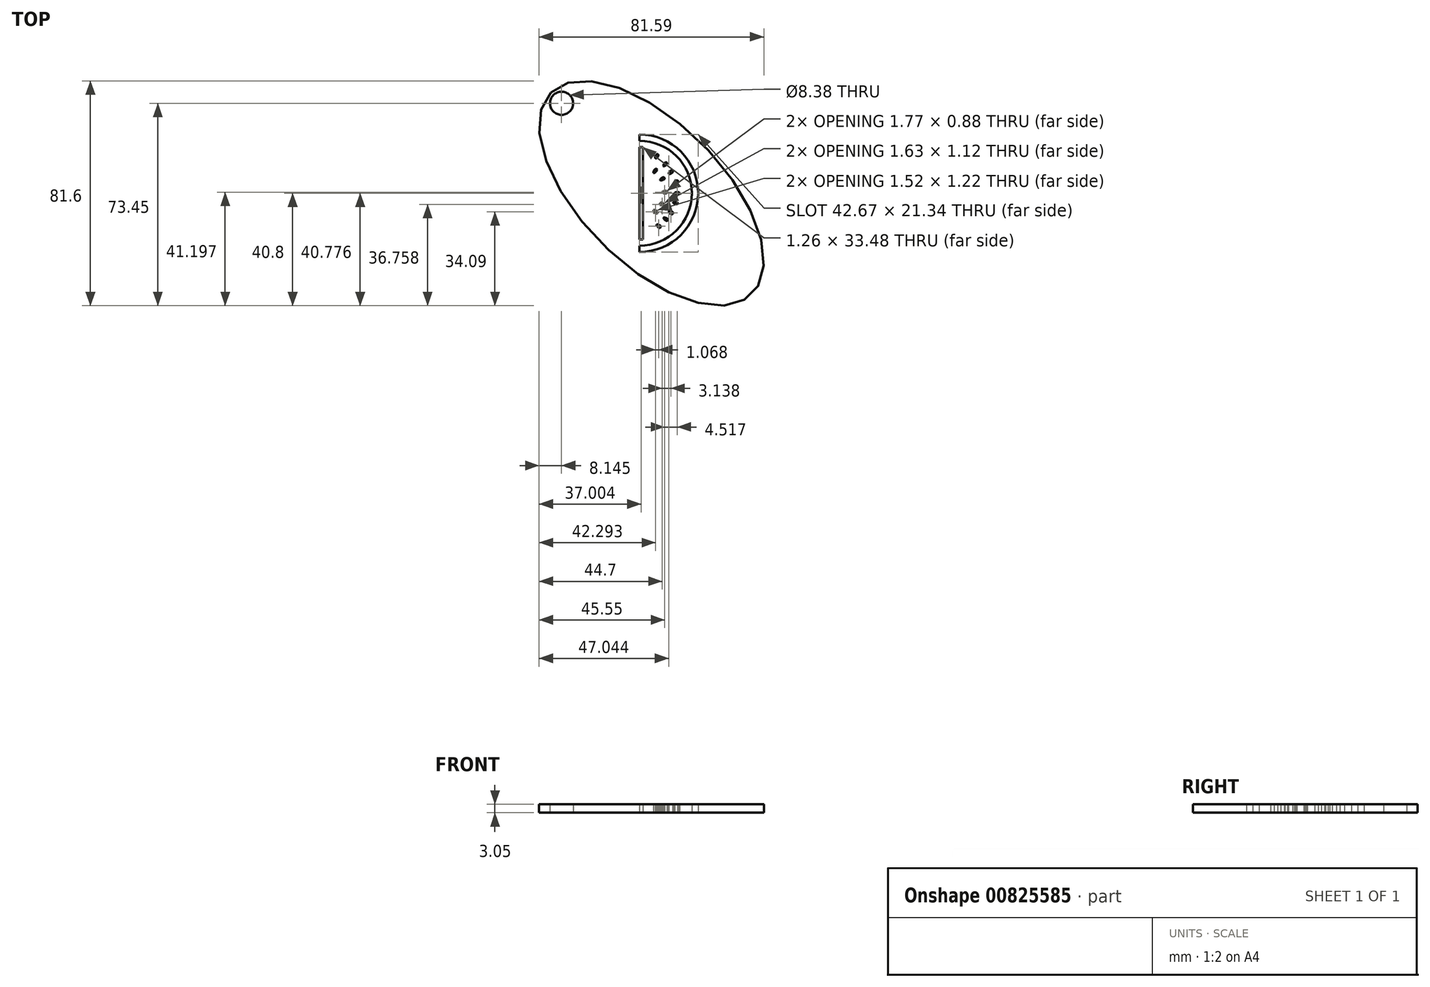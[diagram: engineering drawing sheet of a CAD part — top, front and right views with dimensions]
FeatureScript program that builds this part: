
annotation { "Feature Type Name" : "Feature", "Feature Type Description" : "" }
export const myFeature = defineFeature(function(context is Context, id is Id, definition is map)
    precondition{}
    {
        {
            var Q0;
            Q0=qCreatedBy(makeId("Top.planeOp"),FACE);
            var sketch = newSketch(context, id + "F0", { "sketchPlane" : qUnion([Q0])});
            skCircle(sketch, "E0", {"center": v(0, 0) * mm, "radius": 35.56 * mm});
            skCircle(sketch, "E1", {"center": v(0, 0) * mm, "radius": 31.75 * mm});
            skCircle(sketch, "E2", {"center": v(0, 0) * mm, "radius": 27.94 * mm, "construction": true});
            skLineSegment(sketch, "E3", {"start": v(-35.56, 0) * mm, "end": v(-31.75, 0) * mm, "construction": true});
            skLineSegment(sketch, "E4", {"start": v(-31.75, 0) * mm, "end": v(-27.94, 0) * mm, "construction": true});
            skLineSegment(sketch, "E5", {"start": v(0, 0) * mm, "end": v(0, 27.94) * mm});
            skLineSegment(sketch, "E6", {"start": v(0, -35.56) * mm, "end": v(0, -31.75) * mm});
            skLineSegment(sketch, "E7", {"start": v(0, -31.75) * mm, "end": v(0, -27.94) * mm});
            skLineSegment(sketch, "E8", {"start": v(0, -27.94) * mm, "end": v(0, 0) * mm});
            skLineSegment(sketch, "E9", {"start": v(0, 35.56) * mm, "end": v(0, 31.75) * mm});
            skLineSegment(sketch, "E10", {"start": v(0, 31.75) * mm, "end": v(0, 27.94) * mm});
            skLineSegment(sketch, "E11.bottom", {"start": v(0, 27.94) * mm, "end": v(0, 27.94) * mm});
            skLineSegment(sketch, "E11.top", {"start": v(0, -27.94) * mm, "end": v(0, -27.94) * mm});
            skLineSegment(sketch, "E11.left", {"start": v(0, 27.94) * mm, "end": v(0, -27.94) * mm});
            skLineSegment(sketch, "E11.right", {"start": v(0, 27.94) * mm, "end": v(0, -27.94) * mm});
            skLineSegment(sketch, "E12", {"start": v(0, 0) * mm, "end": v(17.78, 0) * mm, "construction": true});
            skLineSegment(sketch, "E13", {"start": v(17.78, 0) * mm, "end": v(35.56, 0) * mm, "construction": true});
            skLineSegment(sketch, "E14", {"start": v(0, 35.56) * mm, "end": v(-35.56, 0) * mm, "construction": true});
            skLineSegment(sketch, "E15", {"start": v(-35.56, 0) * mm, "end": v(0, -35.56) * mm, "construction": true});
            skLineSegment(sketch, "E16", {"start": v(7.36, -42.92) * mm, "end": v(50.29, 0) * mm, "construction": true});
            skLineSegment(sketch, "E17", {"start": v(7.36, 42.92) * mm, "end": v(50.29, 0) * mm, "construction": true});
            skLineSegment(sketch, "E18", {"start": v(0, -35.56) * mm, "end": v(7.36, -42.92) * mm, "construction": true});
            skLineSegment(sketch, "E19", {"start": v(0, 35.56) * mm, "end": v(7.36, 42.92) * mm, "construction": true});
            skLineSegment(sketch, "E20", {"start": v(7.36, -42.92) * mm, "end": v(7.36, 42.92) * mm, "construction": true});
            skPoint(sketch, "E21", {"position": v(7.36, 0) * mm});
            skLineSegment(sketch, "E22", {"start": v(7.36, 0) * mm, "end": v(37.6, 30.24) * mm, "construction": true});
            skLineSegment(sketch, "E23", {"start": v(7.36, 0) * mm, "end": v(-22.87, -30.24) * mm, "construction": true});
            skLineSegment(sketch, "E24", {"start": v(7.36, 0) * mm, "end": v(68.27, -60.9) * mm, "construction": true});
            skLineSegment(sketch, "E25.bottom", {"start": v(0, -27.94) * mm, "end": v(2.1, -27.94) * mm});
            skLineSegment(sketch, "E25.top", {"start": v(0, 27.86) * mm, "end": v(2.1, 27.86) * mm});
            skLineSegment(sketch, "E25.left", {"start": v(0, -27.94) * mm, "end": v(0, 27.86) * mm});
            skLineSegment(sketch, "E25.right", {"start": v(2.1, -27.94) * mm, "end": v(2.1, 27.86) * mm});
            skPoint(sketch, "E26", {"position": v(-22.87, -30.24) * mm});
            skPoint(sketch, "E27", {"position": v(37.6, 30.24) * mm});
            skPoint(sketch, "E28", {"position": v(-53.54, 60.9) * mm});
            skPoint(sketch, "E29", {"position": v(68.27, -60.9) * mm});
            skEllipse(sketch, "E30", {"center": v(7.36, 0) * mm, "majorRadius": 86.13 * mm, "minorRadius": 42.76 * mm, "majorAxis": v(-0.7, 0.7)});
            skFitSpline(sketch, "E31", {"points": [v(10.37, -18.9) * mm, v(11.47, -20.6) * mm, v(12.55, -20.89) * mm, v(12.77, -19.78) * mm, v(10.37, -18.9) * mm]});
            skFitSpline(sketch, "E32", {"points": [v(17.74, -11.01) * mm, v(19.11, -12.49) * mm, v(20.23, -12.58) * mm, v(20.26, -11.46) * mm, v(17.74, -11.01) * mm]});
            skFitSpline(sketch, "E33", {"points": [v(14.63, -14.82) * mm, v(15.87, -16.4) * mm, v(16.98, -16.6) * mm, v(17.1, -15.49) * mm, v(14.63, -14.82) * mm]});
            skFitSpline(sketch, "E34", {"points": [v(20.26, -5.4) * mm, v(21.92, -6.53) * mm, v(23.03, -6.38) * mm, v(22.8, -5.28) * mm, v(20.26, -5.4) * mm]});
            skFitSpline(sketch, "E35", {"points": [v(21.34, 0) * mm, v(23.21, -0.75) * mm, v(24.26, -0.37) * mm, v(23.81, 0.66) * mm, v(21.34, 0) * mm]});
            skFitSpline(sketch, "E36", {"points": [v(20.86, 5.99) * mm, v(22.85, 6.27) * mm, v(23.57, 7.13) * mm, v(22.66, 7.8) * mm, v(20.86, 5.99) * mm]});
            skFitSpline(sketch, "E37", {"points": [v(8.6, -10.17) * mm, v(9.69, -11.86) * mm, v(10.77, -12.15) * mm, v(11, -11.05) * mm, v(8.6, -10.17) * mm]});
            skFitSpline(sketch, "E38", {"points": [v(12.51, -5.96) * mm, v(13.88, -7.43) * mm, v(15, -7.53) * mm, v(15.03, -6.4) * mm, v(12.51, -5.96) * mm]});
            skFitSpline(sketch, "E39", {"points": [v(13.82, 0.66) * mm, v(15.68, -0.1) * mm, v(16.74, 0.29) * mm, v(16.28, 1.32) * mm, v(13.82, 0.66) * mm]});
            skFitSpline(sketch, "E40", {"points": [v(12.55, 8) * mm, v(14.56, 8.19) * mm, v(15.32, 9.01) * mm, v(14.44, 9.72) * mm, v(12.55, 8) * mm]});
            skFitSpline(sketch, "E41", {"points": [v(17.78, 11.72) * mm, v(19.7, 12.35) * mm, v(20.25, 13.32) * mm, v(19.25, 13.81) * mm, v(17.78, 11.72) * mm]});
            skFitSpline(sketch, "E42", {"points": [v(14.6, 16.37) * mm, v(16.38, 17.31) * mm, v(16.76, 18.37) * mm, v(15.68, 18.68) * mm, v(14.6, 16.37) * mm]});
            skFitSpline(sketch, "E43", {"points": [v(8.6, 12.31) * mm, v(10.33, 13.32) * mm, v(10.68, 14.4) * mm, v(9.59, 14.66) * mm, v(8.6, 12.31) * mm]});
            skFitSpline(sketch, "E44", {"points": [v(9.69, 21.06) * mm, v(11.27, 22.3) * mm, v(11.47, 23.4) * mm, v(10.35, 23.52) * mm, v(9.69, 21.06) * mm]});
            skLineSegment(sketch, "E45", {"start": v(-53.54, 60.9) * mm, "end": v(-52, 59.36) * mm});
            skLineSegment(sketch, "E46", {"start": v(-53.54, 60.9) * mm, "end": v(7.36, 0) * mm, "construction": true});
            skCircle(sketch, "E47", {"center": v(-47.05, 54.42) * mm, "radius": 6.99 * mm});
            skSolve(sketch);
        }
        {
            var Q0;
            Q0=makeQuery(id+"F0.imprint","IMPRINT",FACE,{"disambiguationData":[TD([[makeQuery(id+"F0.imprint","IMPRINT",EDGE,{"derivedFrom":sQuery(id+"F0.wireOp",EDGE,"E30")}),1.0]])]});
            var Q1;
            {var subQ0=sQuery(id+"F0.wireOp",EDGE,"E6");Q1=makeQuery(id+"F0.imprint","IMPRINT",FACE,{"disambiguationData":[TD([[makeQuery(id+"F0.imprint","IMPRINT",EDGE,{"derivedFrom":subQ0}),1.0]])]});}
            var Q2;
            {var subQ0=sQuery(id+"F0.wireOp",EDGE,"E7");Q2=makeQuery(id+"F0.imprint","IMPRINT",FACE,{"disambiguationData":[TD([[makeQuery(id+"F0.imprint","IMPRINT",EDGE,{"derivedFrom":subQ0}),1.0]])]});}
            var Q3;
            {var subQ1=sQuery(id+"F0.wireOp",EDGE,"E7");Q3=makeQuery(id+"F0.imprint","IMPRINT",FACE,{"disambiguationData":[TD([[makeQuery(id+"F0.imprint","IMPRINT",EDGE,{"derivedFrom":subQ1}),-1.0]])]});}
            extrude(context, id + "F1", {"entities" : qUnion([Q0, Q1, Q2, Q3]), "depth" : 5.08 * mm, "offsetDistance" : 25.4 * mm});
        }
        {
            var Q0;
            Q0=makeQuery(id+"F1.opExtrude","SWEPT_BODY",BODY,{"disambiguationData":[OSD([sQuery(id+"F0.wireOp",EDGE,"E0"),sQuery(id+"F0.wireOp",EDGE,"E1"),sQuery(id+"F0.wireOp",EDGE,"E6"),sQuery(id+"F0.wireOp",EDGE,"E9"),sQuery(id+"F0.wireOp",EDGE,"E25.bottom"),sQuery(id+"F0.wireOp",EDGE,"E25.top"),sQuery(id+"F0.wireOp",EDGE,"E25.left"),sQuery(id+"F0.wireOp",EDGE,"E25.right"),sQuery(id+"F0.wireOp",EDGE,"E30"),sQuery(id+"F0.wireOp",EDGE,"E31"),sQuery(id+"F0.wireOp",EDGE,"E32"),sQuery(id+"F0.wireOp",EDGE,"E33"),sQuery(id+"F0.wireOp",EDGE,"E34"),sQuery(id+"F0.wireOp",EDGE,"E35"),sQuery(id+"F0.wireOp",EDGE,"E36"),sQuery(id+"F0.wireOp",EDGE,"E37"),sQuery(id+"F0.wireOp",EDGE,"E38"),sQuery(id+"F0.wireOp",EDGE,"E39"),sQuery(id+"F0.wireOp",EDGE,"E40"),sQuery(id+"F0.wireOp",EDGE,"E41"),sQuery(id+"F0.wireOp",EDGE,"E42"),sQuery(id+"F0.wireOp",EDGE,"E43"),sQuery(id+"F0.wireOp",EDGE,"E44")])]});
            var Q1;
            Q1=sQuery(id+"F0.wireOp",VERTEX,"E21");
            transform(context, id + "F2", {"entities" : qUnion([Q0]), "transformType" : TransformType.SCALE_UNIFORMLY, "scale" : 0.6, "scalePoint" : qUnion([Q1]), "makeCopy" : false});
        }
    });
